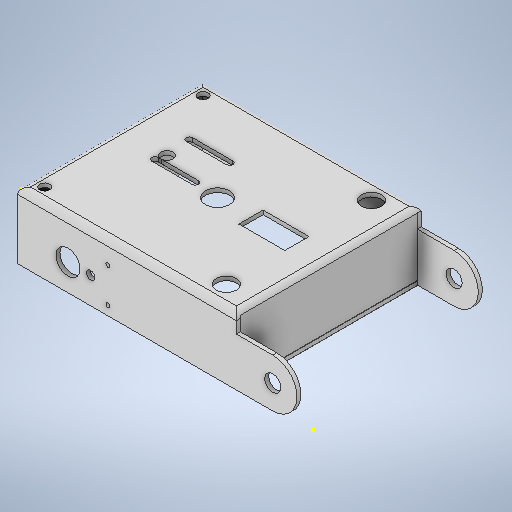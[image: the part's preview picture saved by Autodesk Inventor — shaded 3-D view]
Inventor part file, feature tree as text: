
AUTODESK INVENTOR PART (.ipt)
format: ipt  version: 2025 (Build 290162010, 162A)  size: 516,608 bytes
history: native  units: in
note: dims shown in document units (in); Inventor stores cm internally (conversion verified against a paired STEP export)
features: sketch x28, extrude x26, thicken_offset x2, fillet x1
ambient origin geometry x8: Origin, YZ Plane, XZ Plane, XY Plane, X Axis, Y Axis, Z Axis, Center Point
bodies: Solid1 (feature_tree)
feature tree (57):
  extrude  "Extrusion1"  Depth=0.0787in
  extrude  "Extrusion2"  Depth=0.0787in TaperAngle=0.0deg
  extrude  "Extrusion3"  Depth=0.0787in TaperAngle=0.0deg
  extrude  "Extrusion4"  Depth=0.7087in
  sketch  "Sketch7"  dims[d35=0.0787in d36=0.0in d37=0.315in]
  extrude  "Extrusion5"  Depth=0.0787in
  extrude  "Extrusion6"  Depth=0.0787in TaperAngle=0.0deg
  sketch  "Sketch10"  dims[d48=0.0787in d49=0.0in d50=0.0787in d51=0.0in]
  sketch  "Sketch11"  dims[d52=0.5906in d53=1.1102in]
  extrude  "Extrusion7"  Depth=0.0787in TaperAngle=0.0deg
  extrude  "Extrusion8"  Depth=0.0787in TaperAngle=0.0deg
  extrude  "Extrusion9"  Depth=0.5906in
  extrude  "Extrusion10"  Depth=0.4724in
  extrude  "Extrusion11"  Depth=0.8976in
  extrude  "Extrusion12"  Depth=0.125in
  fillet  "Fillet1"  Radius=0.0787in
  extrude  "Extrusion13"  Depth=0.0787in
  extrude  "Extrusion14"  Depth=0.5906in
  extrude  "Extrusion16"  Depth=0.3937in
  sketch  "Sketch21"  dims[d77=0.0787in d78=0.0in d79=0.0787in d80=0.0in]
  sketch  "Sketch22"  dims[d81=0.0787in d82=0.0in d83=0.0787in]
  extrude  "Extrusion17"  Depth=0.5906in
  extrude  "Extrusion18"  Depth=1.2205in TaperAngle=0.0deg
  extrude  "Extrusion19"  Depth=0.0787in TaperAngle=0.0deg
  thicken_offset  "Thicken1"
  thicken_offset  "Thicken2"
  extrude  "Extrusion20"  Depth=0.0787in
  sketch  "Sketch28"  dims[d88=0.1181in d89=0.1969in]
  extrude  "Extrusion24"  Depth=0.0787in
  extrude  "Extrusion25"  Depth=0.2362in
  extrude  "Extrusion26"  Depth=0.1969in
  extrude  "Extrusion27"  Depth=0.1181in
  extrude  "Extrusion28"  Depth=0.1181in
  extrude  "Extrusion29"  Depth=0.6693in
  extrude  "Extrusion30"  Depth=0.063in
  sketch  "Sketch1"  dims[d2=0.0787in d3=0.0in d4=1.4173in]
  sketch  "Sketch2"  dims[d5=0.9449in d6=0.0787in d7=0.0in]
  sketch  "Sketch5"  dims[d29=0.0787in d30=0.0in d31=0.0787in d32=0.0in]
  sketch  "Sketch6"  dims[d33=0.7087in d34=0.7087in]
  sketch  "Sketch8"  dims[d38=0.0787in d39=0.0in d42=0.0787in d43=0.0in]
  sketch  "Sketch9"  dims[d44=0.0787in d45=0.0in d46=0.0787in d47=0.0in]
  sketch  "Sketch12"  dims[d54=0.4724in d55=0.315in]
  sketch  "Sketch13"  dims[d56=0.8976in d57=0.6299in]
  sketch  "Sketch14"  dims[d58=0.0787in d59=0.0in d60=0.125in d61=0.0787in]
  sketch  "Sketch15"  dims[d62=1.2205in d63=0.0in d64=0.0787in]
  sketch  "Sketch16"  dims[d65=1.2205in d66=0.0in d69=0.5906in]
  sketch  "Sketch17"  dims[d70=0.3937in d71=0.3937in]
  sketch  "Sketch18"  dims[d72=0.3937in d73=0.5906in]
  sketch  "Sketch20"  dims[d74=0.3937in d75=1.2205in d76=0.0in]
  sketch  "Sketch23"  dims[d84=0.0787in d85=0.0787in]
  sketch  "Sketch24"  dims[d86=0.0787in d87=0.2362in]
  sketch  "Sketch29"  dims[d90=0.1969in d91=0.1181in]
  sketch  "Sketch30"  dims[d92=0.1181in d93=0.748in]
  sketch  "Sketch31"  dims[d94=0.315in d95=0.6693in]
  sketch  "Sketch32"  dims[d96=0.063in d97=0.7874in]
  sketch  "Sketch33"  dims[d98=0.126in]
  sketch  "Sketch34"  dims[d99=0.063in d100=0.7874in d101=0.126in d102=0.1181in d103=0.1181in d104=0.063in d105=0.2362in d106=0.0787in d107=0.0in d119=0.2126in d120=0.4429in d121=0.4429in d122=0.1654in d123=1.0in d124=0.0in d125=0.3386in d127=0.3406in d128=0.3406in d129=0.0787in d130=0.0787in d131=1.0in d132=0.0in d133=0.4429in d134=0.0787in d135=0.0787in d136=1.0in d137=0.0in d138=1.0in d139=0.0in d140=1.0in d141=0.0in d142=0.1969in d143=0.1969in d144=0.1969in d145=0.1969in d146=1.0in d147=0.0in d148=3.0in d149=3.0in d150=0.0in d151=0.0in]
